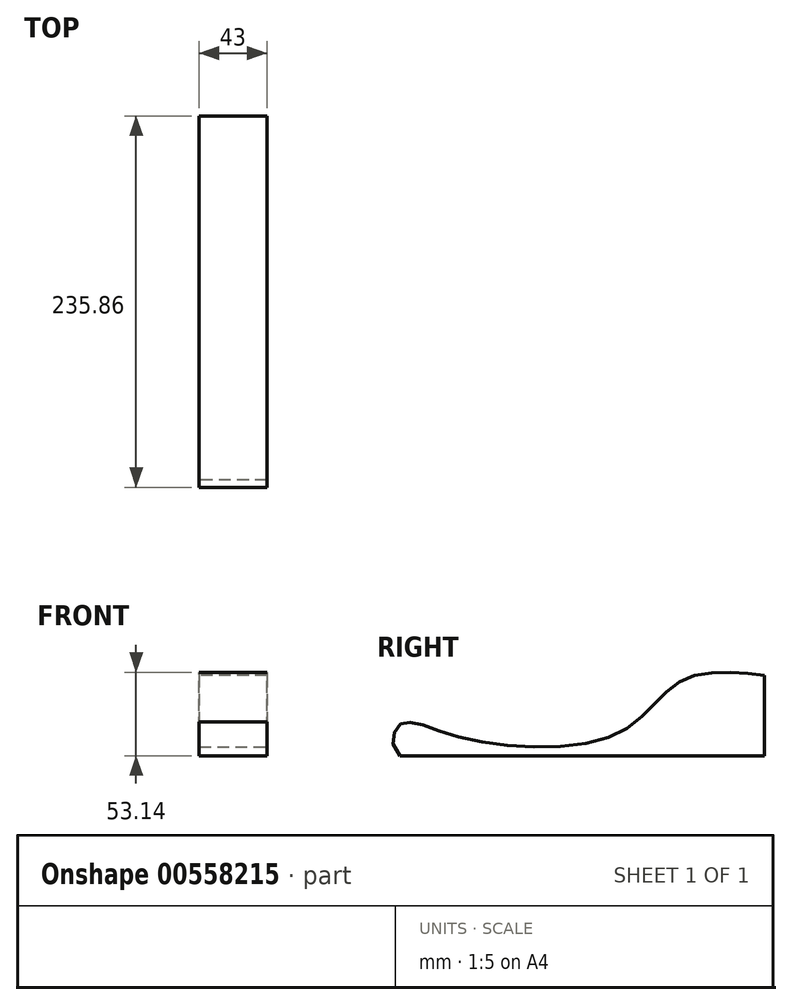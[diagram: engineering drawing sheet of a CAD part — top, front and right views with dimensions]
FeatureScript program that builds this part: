
annotation { "Feature Type Name" : "Feature", "Feature Type Description" : "" }
export const myFeature = defineFeature(function(context is Context, id is Id, definition is map)
    precondition{}
    {
        {
            var Q0;
            Q0=qCreatedBy(makeId("Right.planeOp"),FACE);
            var sketch = newSketch(context, id + "F0", { "sketchPlane" : qUnion([Q0])});
            skLineSegment(sketch, "E0", {"start": v(92.45, 31.06) * mm, "end": v(92.45, -19.95) * mm});
            skLineSegment(sketch, "E1", {"start": v(92.45, -19.95) * mm, "end": v(-138.9, -19.95) * mm});
            skFitSpline(sketch, "E2", {"points": [v(-138.9, -19.95) * mm, v(-138.9, 0) * mm, v(-103.55, -7.32) * mm, v(0, -5.3) * mm, v(41.42, 28.54) * mm, v(92.45, 31.06) * mm], "startDerivative": vector(-166.98, 154.86) * mm, "endDerivative": vector(217.92, -29.02) * mm});
            skSolve(sketch);
        }
        {
            var Q0;
            Q0=makeQuery(id+"F0.imprint","IMPRINT",FACE,{"disambiguationData":[TD([[makeQuery(id+"F0.imprint","IMPRINT",EDGE,{"derivedFrom":sQuery(id+"F0.wireOp",EDGE,"E0")}),-1.0]])]});
            extrude(context, id + "F1", {"entities" : qUnion([Q0]), "depth" : 43 * mm, "offsetDistance" : 25 * mm});
        }
        {
            var Q0;
            Q0=makeQuery(id+"F1.opExtrude","SWEPT_BODY",BODY,{"disambiguationData":[OSD([sQuery(id+"F0.wireOp",EDGE,"E0"),sQuery(id+"F0.wireOp",EDGE,"E1"),sQuery(id+"F0.wireOp",EDGE,"E2")])]});
            transform(context, id + "F2", {"entities" : qUnion([Q0]), "transformType" : TransformType.TRANSLATION_3D, "dx" : 0 * mm, "dy" : 0 * mm, "dz" : 21 * mm, "makeCopy" : false});
        }
        {
            var Q0;
            Q0=makeQuery(id+"F1.opExtrude","SWEPT_BODY",BODY,{"disambiguationData":[OSD([sQuery(id+"F0.wireOp",EDGE,"E0"),sQuery(id+"F0.wireOp",EDGE,"E1"),sQuery(id+"F0.wireOp",EDGE,"E2")])]});
            transform(context, id + "F3", {"entities" : qUnion([Q0]), "transformType" : TransformType.TRANSLATION_3D, "dx" : 0 * mm, "dy" : 0 * mm, "dz" : 0 * mm, "makeCopy" : true});
        }
        {
            var Q0;
            Q0=makeQuery(id+"F3.opPattern","COPY",BODY,{"derivedFrom":makeQuery(id+"F1.opExtrude","SWEPT_BODY",BODY,{"disambiguationData":[OSD([sQuery(id+"F0.wireOp",EDGE,"E0"),sQuery(id+"F0.wireOp",EDGE,"E1"),sQuery(id+"F0.wireOp",EDGE,"E2")])]}),"instanceName":"1"});
            deleteBodies(context, id + "F4", {"entities" : qUnion([Q0])});
        }
    });
